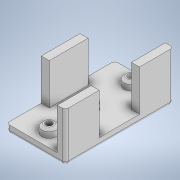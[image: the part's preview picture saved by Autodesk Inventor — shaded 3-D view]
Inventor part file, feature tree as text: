
AUTODESK INVENTOR PART (.ipt)
format: ipt  version: 2020 (Build 240168000, 168)  size: 210,944 bytes
history: native  units: in
note: dims shown in document units (in); Inventor stores cm internally (conversion verified against a paired STEP export)
features: extrude x6, sketch x6, fillet x2, chamfer x1
ambient origin geometry x8: Origin, YZ Plane, XZ Plane, XY Plane, X Axis, Y Axis, Z Axis, Center Point
bodies: Solid1 (feature_tree)
feature tree (15):
  extrude  "Extrusion1"  Depth=2.6378in
  extrude  "Extrusion2"  Depth=0.1969in
  fillet  "Fillet2"  Radius=0.8268in
  extrude  "Extrusion6"  Depth=0.8268in
  fillet  "Fillet3"  Radius=1.0in
  extrude  "Extrusion8"  Depth=0.1969in
  chamfer  "Chamfer1"  Distance=1.0in
  extrude  "Extrusion9"  Depth=0.0197in
  extrude  "Extrusion10"  Depth=0.0197in
  sketch  "Sketch1"  dims[d0=1.4331in d1=2.6378in]
  sketch  "Sketch2"  dims[d2=0.1969in d3=0.0in d4=0.1969in d5=0.8268in]
  sketch  "Sketch6"  dims[d6=0.1969in d7=0.8268in d8=1.0in d9=0.0in]
  sketch  "Sketch8"  dims[d25=0.0787in d26=0.1969in]
  sketch  "Sketch9"  dims[d27=0.9449in d28=1.0in d29=0.0in]
  sketch  "Sketch10"  dims[d36=0.0787in d37=0.3406in d38=0.3406in d39=0.3406in d40=0.1969in d41=0.0in d42=0.0591in d43=0.0787in d44=45.0deg d45=0.1575in d46=0.1575in d47=0.1575in d48=0.7874in d49=0.0in d50=0.2362in d51=0.2362in d52=0.2362in d53=0.0984in d54=0.0in d10=0.0197in d11=0.0344in d13=0.0197in d14=0.0344in d15=0.0197in d16=0.0344in]
